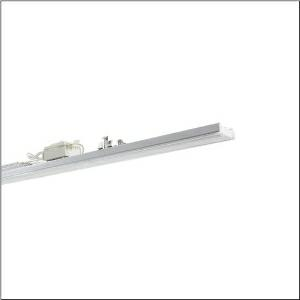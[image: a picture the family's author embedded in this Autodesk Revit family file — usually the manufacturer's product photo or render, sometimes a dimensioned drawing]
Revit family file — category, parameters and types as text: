
# Revit family: licross_r__11_recessed_ho_51te12dv4m2m_f321
name_source: partatom
category: Lighting Fixtures
units: mm (PartAtom-declared; Revit-internal decimal feet)

## family parameters
Cut with Voids When Loaded = No
Host = Face
Light Source = No
Part Type = Normal
Room Calculation Point = No
Round Connector Dimension = Use Diameter
Shared = No

## types (1)
- --- (1 x LED, 27150 lm, 150.5 W, 4000K)
    Apparent Load = 150 VA
    CIE Flux Codes = 66 91 98 100 100
    Color Rendering = 80
    Color Temperature = 4000K
    Default Elevation = 1800 mm
    Description = Licross® 11 Recessed HO, luminaire insert, of sheet steel, galvanised, coil coated, white, length: 2.250mm, width: 66mm, height: 67mm, LED rated luminous flux: 27.150lm, light colour: 840, control gear: DALI 2, with plug, 5-pole, with phase selection, mains connection: 220..240V, AC, 50/60Hz, rated input power: 151W, internal wiring halogen-free, primary optical cover: cover, of PMMA, light emission: direct distribution, primary light characteristic: symmetric, protection rating (complete): IP54, insulation class (complete): insulation class I (protective earthing), certification: CE, ENEC, VDE, UKCA, protection symbol: D if used in an environment with non-conductive dust loads with corresponding accessories, impact resistance: IK06, permissible ambient temperature for indoor applications: -40..+35°C, corresponds to IFS (International Featured Standards) requirements for safety and quality in the food industry, reducing of maximum allowable ambient temperature of 5°C with ceiling mounting, LABS conformity tested according to VDMA 24364:2018-05, packaging unit: 1 piece
    Height = 58 mm
    Lamp = 1 x LED
    Lamp Light Flux = 27150 lm
    Lamp Power = 150.5 W
    Lamp count = 1
    Length = 2250 mm
    Luminous efficacy = 180 lm/W
    Manufacturer = Siteco
    ModVariant = No
    Model = 51TE12DV4M2M
    Mounting Place = Ceiling
    Mounting Type = Pendant
    Number of Poles = 1
    OnlyDefault = Yes
    Power Factor = 1
    Product Name = Licross® 11 Recessed HO
    Product group = luminaire insert | ceiling pendant
    ProductGroupID = 902
    Protection Class = Protection class I
    Protection Degree = IP 54
    RLX_Detail_Level = 1
    RLX_Emergency_Light_Flux = 0 lm
    RLX_Emergency_Type = 0
    RLX_Emergency_Type_DB = No
    RlxData = <blob elided: 29769 chars, md5=4f1753da>
    Socket = socket
    Standby Power = 0 W
    System Light Flux = 27150 lm
    System Power = 150 W
    Type Comments = factory setting: luminous flux: 100 % | dim-lin: 254 | 690 mA
    Type Image = l_1296930.jpg
    URL = http://relux.com
    VarID = @adj_120917
    Voltage = 0 V
    Weight = 0.00 kg
    Width = 66 mm

## geometry (parser evidence)
native form markers: Blend x4, Sweep x9
no freeform markers — native parametric forms only
